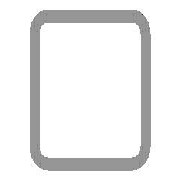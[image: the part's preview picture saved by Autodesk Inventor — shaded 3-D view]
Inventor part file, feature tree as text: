
AUTODESK INVENTOR PART (.ipt)
format: ipt  version: 2016 (Build 200138000, 138)  size: 151,040 bytes
history: native  units: mm (DEFAULTED — no unit token found)
features: other x5, sketch x2, sweep x1, plane x1
ambient origin geometry x8: Origin, YZ Plane, XZ Plane, XY Plane, X Axis, Y Axis, Z Axis, Center Point
bodies: Solid1 (feature_tree), Body (feature_tree)
feature tree (9):
  parser-record x1  (decoder bookkeeping rows leaked as tree rows — omitted from the tree; the rows remain in map.json)
  other  "Driven Length"
  other  "Start plane"
  other  "End plane"
  sweep  "Sweep Path"
  other  "Orientation Work Plane"
  sketch  "Sketch3"  dims[d7=4.0mm d9=60.0mm]
  plane  "Work Plane3"
  sketch  "Sketch4"  dims[d11=60.0mm d12=2.0mm d13=-0.0mm d14=306.305284mm d15=30.0mm d16=30.0mm d17=90.0deg d18=306.305284mm d19=0.0mm d20=0.0mm]
